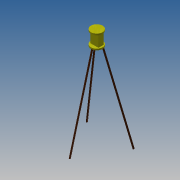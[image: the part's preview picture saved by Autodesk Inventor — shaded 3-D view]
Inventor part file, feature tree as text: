
AUTODESK INVENTOR PART (.ipt)
format: ipt  version: 2014 SP1 (Build 180222100, 222)  size: 124,928 bytes
history: native  units: in
note: dims shown in document units (in); Inventor stores cm internally (conversion verified against a paired STEP export)
features: sketch x7, extrude x5, plane x2, pattern_circular x1
ambient origin geometry x8: Origin, YZ Plane, XZ Plane, XY Plane, X Axis, Y Axis, Z Axis, Center Point
bodies: Solid1 (feature_tree)
feature tree (15):
  extrude  "Extrusion1"  Depth=1.0in TaperAngle=0.0deg
  sketch  "Sketch2"  dims[d3=2.0in d4=75.0deg]
  plane  "Work Plane1"
  sketch  "Sketch3"  dims[d5=1.5in d6=1.5in]
  plane  "Work Plane2"
  extrude  "Extrusion2"  TaperAngle=75.0deg  [1 undecoded]
  extrude  "Extrusion3"  Depth=1.5in
  pattern_circular  "Circular Pattern2"  Count=3 Angle=360.0deg
  extrude  "Extrusion4"  Depth=8.0in
  extrude  "Extrusion6"  Depth=1.0in TaperAngle=0.0deg
  sketch  "Sketch1"  dims[d0=8.0in d1=1.0in d2=0.0in]
  sketch  "Sketch4"  dims[d7=1.0in d8=0.0in]
  sketch  "Sketch5"  dims[d9=1.0in]
  sketch  "Sketch6"  dims[d10=60.0in d11=0.0in d15=1.1811in d16=360.0deg]
  sketch  "Sketch8"  dims[d18=8.0in d19=0.0in d23=8.0in d24=1.0in d25=0.0in]
note: 1 required parameter value undecoded (feature->parameter linkage not recoverable at this tier; creation-order binding heuristic only, values carry confidence <= 0.55)
